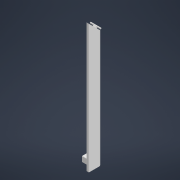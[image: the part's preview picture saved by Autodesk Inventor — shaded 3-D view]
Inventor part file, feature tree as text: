
AUTODESK INVENTOR PART (.ipt)
format: ipt  version: 2021 (Build 250183000, 183)  size: 226,304 bytes
history: native  units: mm
features: extrude x8, sketch x8, other x5, plane x3, fillet x3, reference x2, projected_geometry x2
ambient origin geometry x8: Origin, YZ Plane, XZ Plane, XY Plane, X Axis, Y Axis, Z Axis, Center Point
bodies: Solid1 (feature_tree)
feature tree (31):
  extrude  "Extrusion1"  Depth=5.0mm
  extrude  "Extrusion2"  TaperAngle=45.0deg  [1 undecoded]
  sketch  "Sketch4"  dims[d6=0.0mm d7=0.0mm d8=5.0mm]
  plane  "Work Plane1"
  extrude  "Extrusion3"  Depth=5.0mm
  sketch  "Sketch5"  dims[d9=0.2mm d10=250.0mm d11=0.0mm]
  plane  "Work Plane2"
  plane  "Work Plane3"
  extrude  "Extrusion4"  Depth=250.0mm TaperAngle=0.0deg
  extrude  "Extrusion5"  Depth=10.0mm TaperAngle=0.0deg
  extrude  "Extrusion6"  Depth=1.0mm
  fillet  "Fillet1"  Radius=0.5mm
  fillet  "Fillet2"  Radius=1.0mm
  extrude  "Extrusion8"  Depth=1.0mm
  fillet  "Fillet3"  Radius=10.0mm
  extrude  "Extrusion9"  Depth=10.0mm
  sketch  "Sketch1"  dims[d0=25.0mm d1=5.0mm]
  sketch  "Sketch3"  dims[d2=250.0mm d3=0.0mm d5=45.0deg]
  reference  "Reference1"
  reference  "Reference2"
  sketch  "Sketch6"  dims[d14=10.0mm d15=0.0mm d16=0.3mm d17=0.0mm]
  projected_geometry  "Projected Loop1"
  sketch  "Sketch7"  dims[d18=0.3mm d19=0.0mm d20=5.585054mm d21=0.5mm d22=1.0mm]
  projected_geometry  "Projected Loop2"
  sketch  "Sketch8"  dims[d23=1.0mm d24=1.0mm d27=10.0mm d28=0.0mm]
  sketch  "Sketch9"  dims[d29=1.0mm d30=225.0mm d31=3.2mm d32=56.25mm d33=30.0mm d35=56.25mm d36=10.0mm d38=10.0mm d40=0.0mm d41=0.0mm]
  other  "Assembly1"
  other  "Part3:1"
  other  "<userpath>\green-house\green-house.iam"
  other  "green-house.iam"
  other  "frame-roof:1"
note: 1 required parameter value undecoded (feature->parameter linkage not recoverable at this tier; creation-order binding heuristic only, values carry confidence <= 0.55)
